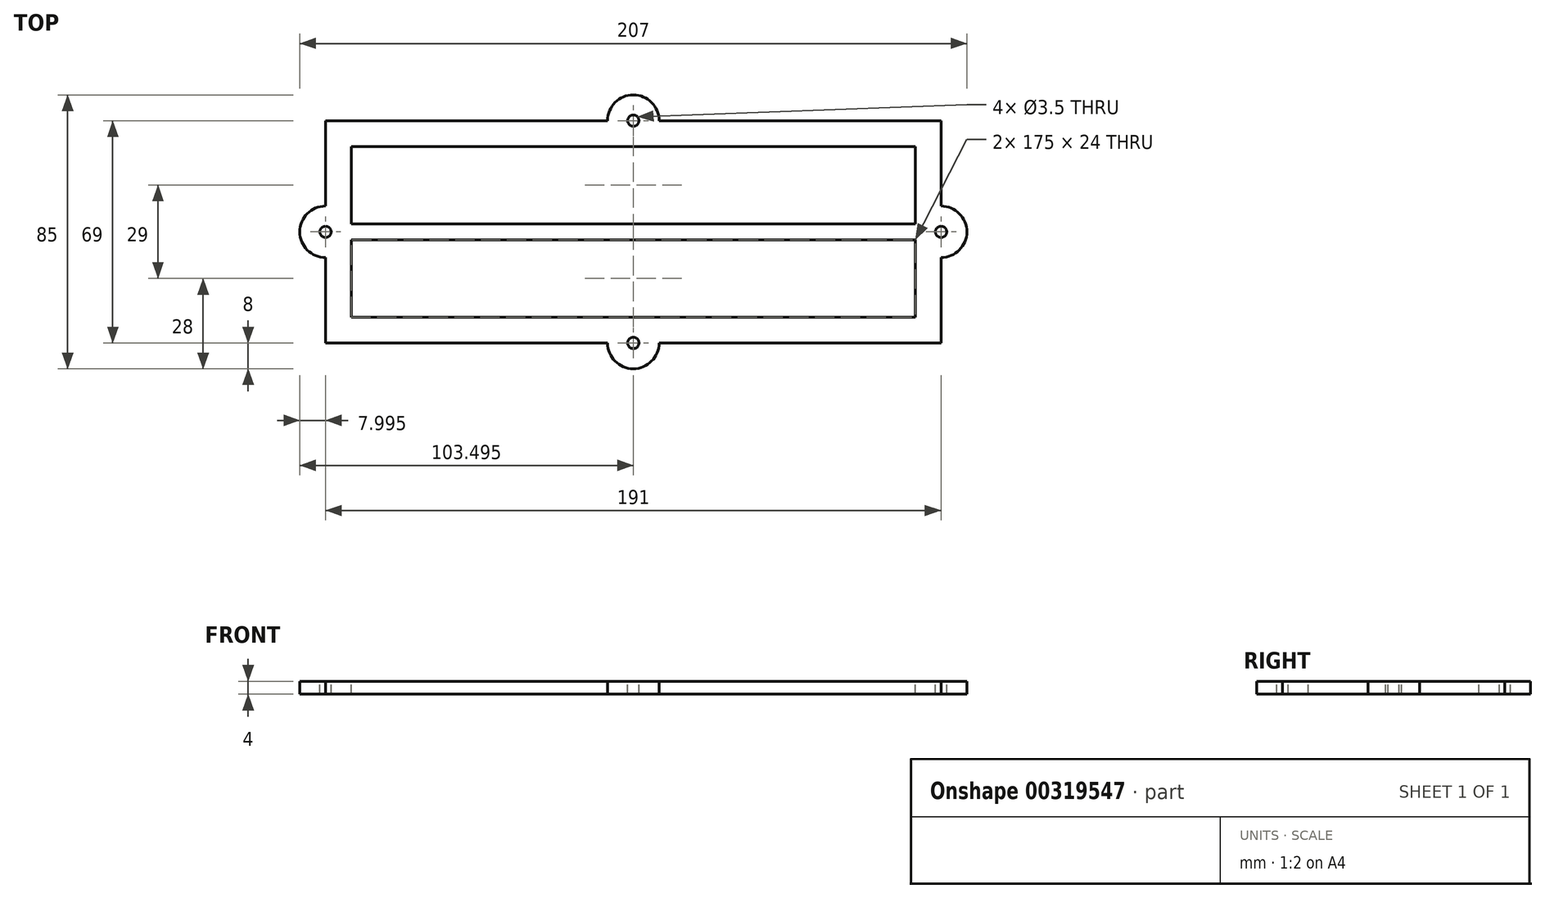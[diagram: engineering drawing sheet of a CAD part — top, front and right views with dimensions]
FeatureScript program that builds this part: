
annotation { "Feature Type Name" : "Feature", "Feature Type Description" : "" }
export const myFeature = defineFeature(function(context is Context, id is Id, definition is map)
    precondition{}
    {
        {
            var Q0;
            Q0=qCreatedBy(makeId("Top.planeOp"),FACE);
            var sketch = newSketch(context, id + "F0", { "sketchPlane" : qUnion([Q0])});
            skLineSegment(sketch, "E0.bottom", {"start": v(-30.8, 43.86) * mm, "end": v(144.2, 43.86) * mm});
            skLineSegment(sketch, "E0.top", {"start": v(-30.8, -9.14) * mm, "end": v(144.2, -9.14) * mm});
            skLineSegment(sketch, "E0.left", {"start": v(-30.8, 43.86) * mm, "end": v(-30.8, -9.14) * mm});
            skLineSegment(sketch, "E0.right", {"start": v(144.2, 43.86) * mm, "end": v(144.2, -9.14) * mm});
            skLineSegment(sketch, "E1.0", {"start": v(-38.8, 51.86) * mm, "end": v(152.2, 51.86) * mm});
            skLineSegment(sketch, "E1.1", {"start": v(-38.8, 51.86) * mm, "end": v(-38.8, -17.14) * mm});
            skLineSegment(sketch, "E1.2", {"start": v(-38.8, -17.14) * mm, "end": v(152.2, -17.14) * mm});
            skLineSegment(sketch, "E1.3", {"start": v(152.2, 51.86) * mm, "end": v(152.2, -17.14) * mm});
            skLineSegment(sketch, "E2.0", {"start": v(-30.8, 14.86) * mm, "end": v(144.2, 14.86) * mm});
            skLineSegment(sketch, "E3.0", {"start": v(-30.8, 19.86) * mm, "end": v(144.2, 19.86) * mm});
            skCircle(sketch, "E4", {"center": v(-38.8, 17.36) * mm, "radius": 8 * mm});
            skCircle(sketch, "E5", {"center": v(-38.8, 17.36) * mm, "radius": 1.75 * mm});
            skCircle(sketch, "E6", {"center": v(152.2, 17.36) * mm, "radius": 8 * mm});
            skCircle(sketch, "E7", {"center": v(152.2, 17.36) * mm, "radius": 1.75 * mm});
            skCircle(sketch, "E8", {"center": v(56.7, -17.14) * mm, "radius": 8 * mm});
            skCircle(sketch, "E9", {"center": v(56.7, -17.14) * mm, "radius": 1.75 * mm});
            skCircle(sketch, "E10", {"center": v(56.7, 51.86) * mm, "radius": 8 * mm});
            skCircle(sketch, "E11", {"center": v(56.7, 51.86) * mm, "radius": 1.75 * mm});
            skSolve(sketch);
        }
        {
            var Q0;
            Q0 = qSketchRegion(id + "F0", true);
            var Q1;
            {var subQ3=sQuery(id+"F0.wireOp",EDGE,"E2.0");Q1=makeQuery(id+"F0.imprint","IMPRINT",FACE,{"disambiguationData":[TD([[makeQuery(id+"F0.imprint","IMPRINT",EDGE,{"derivedFrom":subQ3}),1.0]])]});}
            extrude(context, id + "F1", {"entities" : qUnion([Q0, Q1]), "oppositeDirection" : true, "depth" : 4 * mm});
        }
    });
